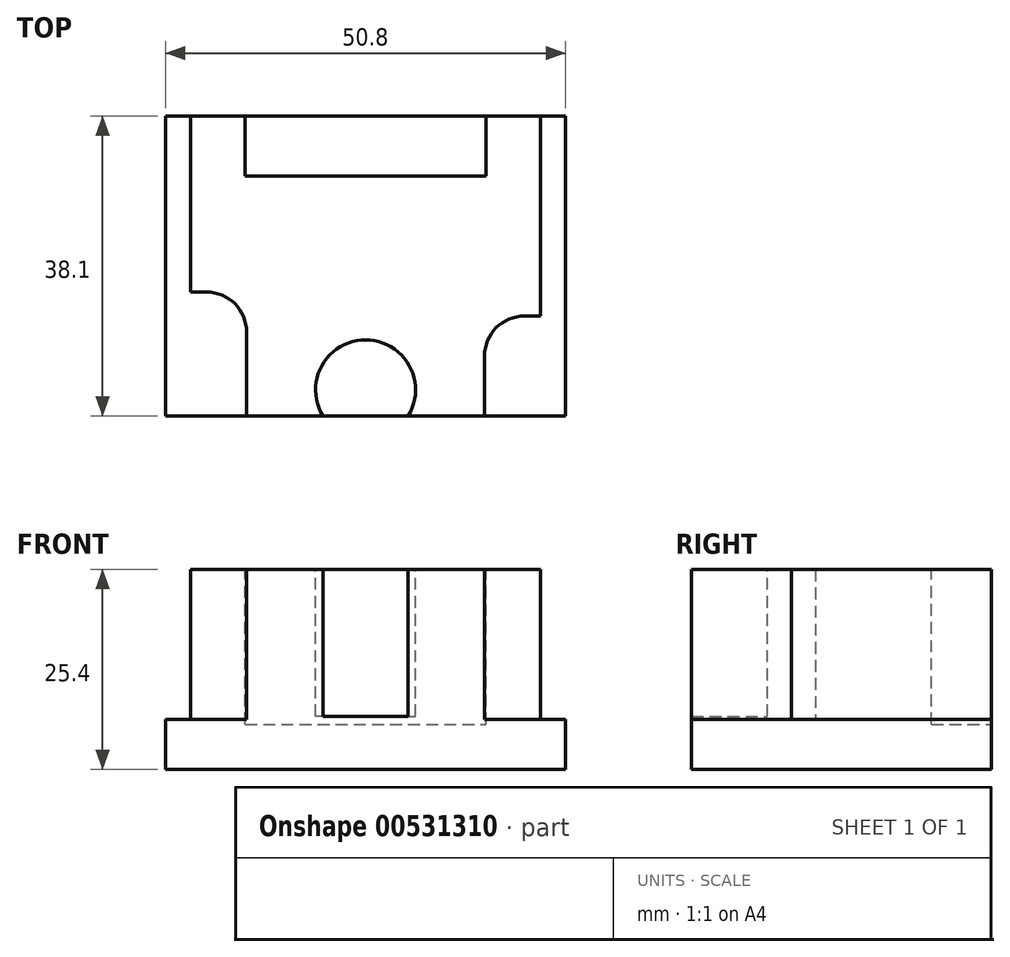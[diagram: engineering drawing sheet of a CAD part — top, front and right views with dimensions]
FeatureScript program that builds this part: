
annotation { "Feature Type Name" : "Feature", "Feature Type Description" : "" }
export const myFeature = defineFeature(function(context is Context, id is Id, definition is map)
    precondition{}
    {
        {
            var Q0;
            Q0=qCreatedBy(makeId("Top.planeOp"),FACE);
            var sketch = newSketch(context, id + "F0", { "sketchPlane" : qUnion([Q0])});
            skLineSegment(sketch, "E0.bottom", {"start": v(25.4, 19.05) * mm, "end": v(-25.4, 19.05) * mm});
            skLineSegment(sketch, "E0.top", {"start": v(25.4, -19.05) * mm, "end": v(-25.4, -19.05) * mm});
            skLineSegment(sketch, "E0.left", {"start": v(25.4, 19.05) * mm, "end": v(25.4, -19.05) * mm});
            skLineSegment(sketch, "E0.right", {"start": v(-25.4, 19.05) * mm, "end": v(-25.4, -19.05) * mm});
            skPoint(sketch, "E0.middle", {"position": v(0, 0) * mm});
            skSolve(sketch);
        }
        {
            var Q0;
            Q0=makeQuery(id+"F0.imprint","IMPRINT",FACE,{"disambiguationData":[TD([[makeQuery(id+"F0.imprint","IMPRINT",EDGE,{"derivedFrom":sQuery(id+"F0.wireOp",EDGE,"E0.bottom")}),1.0]])]});
            extrude(context, id + "F1", {"entities" : qUnion([Q0]), "depth" : 6.35 * mm, "offsetDistance" : 25.4 * mm});
        }
        {
            var Q0;
            Q0=makeQuery(id+"F1.opExtrude","CAP_FACE",FACE,{"disambiguationData":[OSD([sQuery(id+"F0.wireOp",EDGE,"E0.bottom"),sQuery(id+"F0.wireOp",EDGE,"E0.top"),sQuery(id+"F0.wireOp",EDGE,"E0.left"),sQuery(id+"F0.wireOp",EDGE,"E0.right")])],"isStart":false});
            var sketch = newSketch(context, id + "F2", { "sketchPlane" : qUnion([Q0])});
            skLineSegment(sketch, "E1.bottom", {"start": v(22.23, 19.05) * mm, "end": v(-22.22, 19.05) * mm});
            skLineSegment(sketch, "E1.top", {"start": v(22.22, -19.05) * mm, "end": v(-22.23, -19.05) * mm});
            skLineSegment(sketch, "E1.left", {"start": v(22.23, 19.05) * mm, "end": v(22.22, -19.05) * mm});
            skLineSegment(sketch, "E1.right", {"start": v(-22.22, 19.05) * mm, "end": v(-22.23, -19.05) * mm});
            skPoint(sketch, "E1.middle", {"position": v(0, 0) * mm});
            skSolve(sketch);
        }
        {
            var Q0;
            Q0=makeQuery(id+"F2.imprint","IMPRINT",FACE,{"disambiguationData":[TD([[makeQuery(id+"F2.imprint","IMPRINT",EDGE,{"derivedFrom":sQuery(id+"F2.wireOp",EDGE,"E1.bottom")}),1.0]])]});
            extrude(context, id + "F3", {"entities" : qUnion([Q0]), "operationType" : NewBodyOperationType.ADD, "depth" : 19.05 * mm, "offsetDistance" : 25.4 * mm});
        }
        {
            var Q0;
            Q0=qCreatedBy(makeId("Right.planeOp"),FACE);
            var sketch = newSketch(context, id + "F4", { "sketchPlane" : qUnion([Q0])});
            skLineSegment(sketch, "E2.bottom", {"start": v(-22.1, 6.74) * mm, "end": v(-15.75, 6.74) * mm});
            skLineSegment(sketch, "E2.top", {"start": v(-22.1, 25.79) * mm, "end": v(-15.75, 25.79) * mm});
            skLineSegment(sketch, "E2.left", {"start": v(-22.1, 6.74) * mm, "end": v(-22.1, 25.79) * mm});
            skLineSegment(sketch, "E2.right", {"start": v(-15.75, 6.74) * mm, "end": v(-15.75, 25.79) * mm});
            skPoint(sketch, "E2.middle", {"position": v(-18.92, 16.26) * mm});
            skSolve(sketch);
        }
        {
            var Q0;
            Q0=makeQuery(id+"F4.imprint","IMPRINT",FACE,{"disambiguationData":[TD([[makeQuery(id+"F4.imprint","IMPRINT",EDGE,{"derivedFrom":sQuery(id+"F4.wireOp",EDGE,"E2.bottom")}),1.0]])]});
            var Q1;
            Q1=sQuery(id+"F4.wireOp",EDGE,"E2.right");
            revolve(context, id + "F5", {"operationType" : NewBodyOperationType.REMOVE, "entities" : qUnion([Q0]), "axis" : qUnion([Q1]), "revolveType" : RevolveType.FULL, "oppositeDirection" : true});
        }
        {
            var Q0;
            Q0=makeQuery(id+"F3.boolean.opBoolean","MERGE",FACE,{"derivedFrom":[makeQuery(id+"F1.opExtrude","SWEPT_FACE",FACE,{"disambiguationData":[OSD([sQuery(id+"F0.wireOp",EDGE,"E0.bottom")])]}),makeQuery(id+"F3.opExtrude","SWEPT_FACE",FACE,{"disambiguationData":[OSD([sQuery(id+"F2.wireOp",EDGE,"E1.bottom")])]})]});
            var sketch = newSketch(context, id + "F6", { "sketchPlane" : qUnion([Q0])});
            skLineSegment(sketch, "E3.bottom", {"start": v(15.28, 5.72) * mm, "end": v(-15.28, 5.72) * mm});
            skLineSegment(sketch, "E3.top", {"start": v(15.28, 26.04) * mm, "end": v(-15.28, 26.04) * mm});
            skLineSegment(sketch, "E3.left", {"start": v(15.28, 5.72) * mm, "end": v(15.28, 26.04) * mm});
            skLineSegment(sketch, "E3.right", {"start": v(-15.28, 5.72) * mm, "end": v(-15.28, 26.04) * mm});
            skPoint(sketch, "E3.middle", {"position": v(0, 15.88) * mm});
            skPoint(sketch, "E3.middle.positionSnap0", {"position": v(-22.23, 15.88) * mm});
            skPoint(sketch, "E3.centerSnap0", {"position": v(-22.23, 15.88) * mm});
            skSolve(sketch);
        }
        {
            var Q0;
            {var subQ0=sQuery(id+"F6.wireOp",EDGE,"E3.bottom");Q0=makeQuery(id+"F6.imprint","IMPRINT",FACE,{"disambiguationData":[TD([[makeQuery(id+"F6.imprint","IMPRINT",EDGE,{"derivedFrom":subQ0}),-1.0]])]});}
            extrude(context, id + "F7", {"entities" : qUnion([Q0]), "operationType" : NewBodyOperationType.REMOVE, "oppositeDirection" : true, "depth" : 7.62 * mm, "offsetDistance" : 25.4 * mm});
        }
        {
            var Q0;
            Q0=makeQuery(id+"F3.opExtrude","SWEPT_FACE",FACE,{"disambiguationData":[OSD([sQuery(id+"F2.wireOp",EDGE,"E1.right")])]});
            var sketch = newSketch(context, id + "F8", { "sketchPlane" : qUnion([Q0])});
            skLineSegment(sketch, "E4.bottom", {"start": v(3.3, 25.4) * mm, "end": v(19.05, 25.4) * mm});
            skLineSegment(sketch, "E4.top", {"start": v(3.3, 6.35) * mm, "end": v(19.05, 6.35) * mm});
            skLineSegment(sketch, "E4.left", {"start": v(3.3, 25.4) * mm, "end": v(3.3, 6.35) * mm});
            skLineSegment(sketch, "E4.right", {"start": v(19.05, 25.4) * mm, "end": v(19.05, 6.35) * mm});
            skSolve(sketch);
        }
        {
            var Q0;
            Q0=makeQuery(id+"F8.imprint","IMPRINT",FACE,{"disambiguationData":[TD([[makeQuery(id+"F8.imprint","IMPRINT",EDGE,{"derivedFrom":sQuery(id+"F8.wireOp",EDGE,"E4.bottom")}),-1.0]])]});
            extrude(context, id + "F9", {"entities" : qUnion([Q0]), "operationType" : NewBodyOperationType.REMOVE, "oppositeDirection" : true, "depth" : 7.11 * mm, "offsetDistance" : 25.4 * mm});
        }
        {
            var Q0;
            Q0=makeQuery(id+"F3.opExtrude","SWEPT_FACE",FACE,{"disambiguationData":[OSD([sQuery(id+"F2.wireOp",EDGE,"E1.left")])]});
            var sketch = newSketch(context, id + "F10", { "sketchPlane" : qUnion([Q0])});
            skLineSegment(sketch, "E5.bottom", {"start": v(-6.35, 25.4) * mm, "end": v(-19.05, 25.4) * mm});
            skLineSegment(sketch, "E5.top", {"start": v(-6.35, 6.35) * mm, "end": v(-19.05, 6.35) * mm});
            skLineSegment(sketch, "E5.left", {"start": v(-6.35, 25.4) * mm, "end": v(-6.35, 6.35) * mm});
            skLineSegment(sketch, "E5.right", {"start": v(-19.05, 25.4) * mm, "end": v(-19.05, 6.35) * mm});
            skSolve(sketch);
        }
        {
            var Q0;
            Q0=makeQuery(id+"F10.imprint","IMPRINT",FACE,{"disambiguationData":[TD([[makeQuery(id+"F10.imprint","IMPRINT",EDGE,{"derivedFrom":sQuery(id+"F10.wireOp",EDGE,"E5.bottom")}),1.0]])]});
            extrude(context, id + "F11", {"entities" : qUnion([Q0]), "operationType" : NewBodyOperationType.REMOVE, "oppositeDirection" : true, "depth" : 7.11 * mm, "offsetDistance" : 25.4 * mm});
        }
        {
            var Q0;
            Q0=makeQuery(id+"F9.boolean.opBoolean","COPY",EDGE,{"derivedFrom":makeQuery(id+"F9.opExtrude","CAP_EDGE",EDGE,{"disambiguationData":[OSD([sQuery(id+"F8.wireOp",EDGE,"E4.left")])],"isStart":false})});
            fillet(context, id + "F12", {"entities" : qUnion([Q0]), "radius" : 5.08 * mm, "tangentPropagation" : true, "allowEdgeOverflow" : false});
        }
        {
            var Q0;
            Q0=makeQuery(id+"F11.boolean.opBoolean","COPY",EDGE,{"derivedFrom":makeQuery(id+"F11.opExtrude","CAP_EDGE",EDGE,{"disambiguationData":[OSD([sQuery(id+"F10.wireOp",EDGE,"E5.left")])],"isStart":false})});
            fillet(context, id + "F13", {"entities" : qUnion([Q0]), "radius" : 5.08 * mm, "tangentPropagation" : true, "allowEdgeOverflow" : false});
        }
    });
